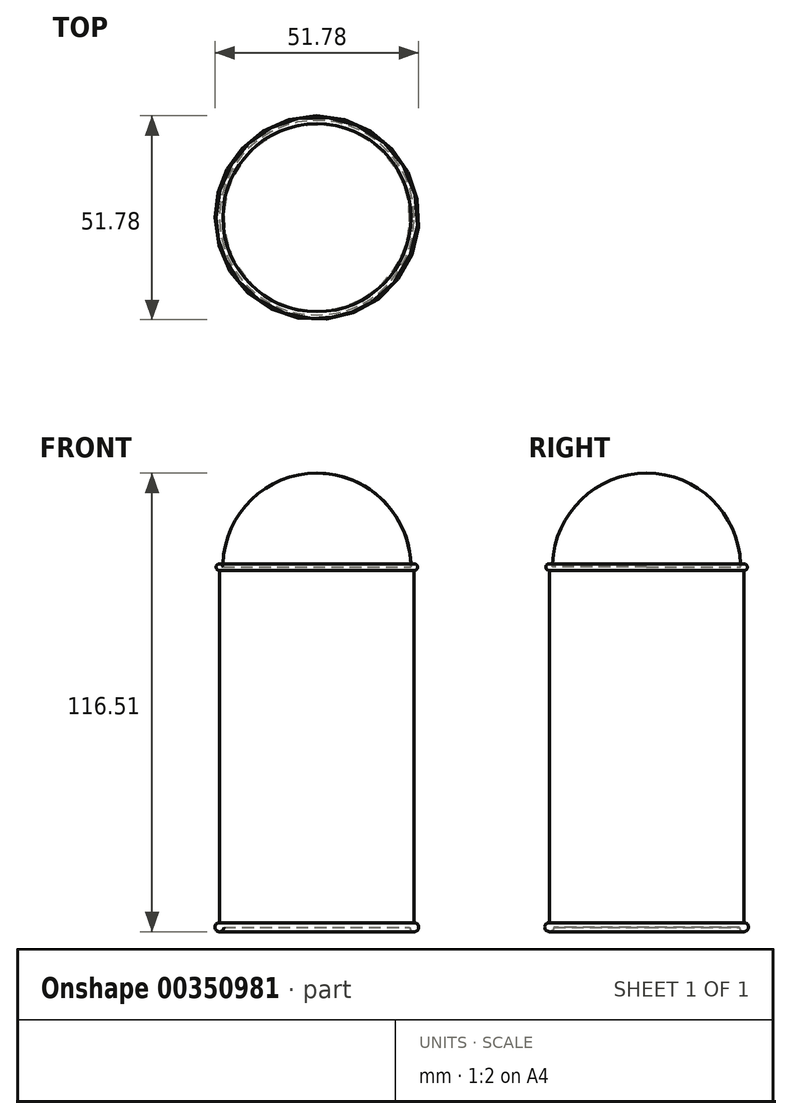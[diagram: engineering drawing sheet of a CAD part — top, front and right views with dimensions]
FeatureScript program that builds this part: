
annotation { "Feature Type Name" : "Feature", "Feature Type Description" : "" }
export const myFeature = defineFeature(function(context is Context, id is Id, definition is map)
    precondition{}
    {
        {
            var Q0;
            Q0=qCreatedBy(makeId("Front.planeOp"),FACE);
            var sketch = newSketch(context, id + "F0", { "sketchPlane" : qUnion([Q0])});
            skLineSegment(sketch, "E0.bottom", {"start": v(0, 0) * mm, "end": v(23.59, 0) * mm});
            skLineSegment(sketch, "E0.left", {"start": v(0, 0) * mm, "end": v(0, 91.47) * mm});
            skLineSegment(sketch, "E0.right", {"start": v(24.74, 1.15) * mm, "end": v(24.74, 90.62) * mm});
            skArc(sketch, "E1", {"start": v(24.74, 90.62) * mm, "mid": v(25.34, 92.08) * mm, "end": v(23.88, 91.47) * mm});
            skArc(sketch, "E2", {"start": v(23.59, 0) * mm, "mid": v(25.55, -0.81) * mm, "end": v(24.74, 1.15) * mm});
            skArc(sketch, "E3", {"start": v(23.88, 91.47) * mm, "mid": v(16.89, 108.36) * mm, "end": v(0, 115.36) * mm});
            skLineSegment(sketch, "E4", {"start": v(0, 115.36) * mm, "end": v(0, 91.47) * mm});
            skSolve(sketch);
        }
        {
            var Q0;
            Q0=makeQuery(id+"F0.imprint","IMPRINT",FACE,{"disambiguationData":[TD([[makeQuery(id+"F0.imprint","IMPRINT",EDGE,{"derivedFrom":sQuery(id+"F0.wireOp",EDGE,"E0.bottom")}),1.0]])]});
            var Q1;
            Q1=sQuery(id+"F0.wireOp",EDGE,"E0.left");
            revolve(context, id + "F1", {"entities" : qUnion([Q0]), "axis" : qUnion([Q1]), "revolveType" : RevolveType.FULL});
        }
    });
